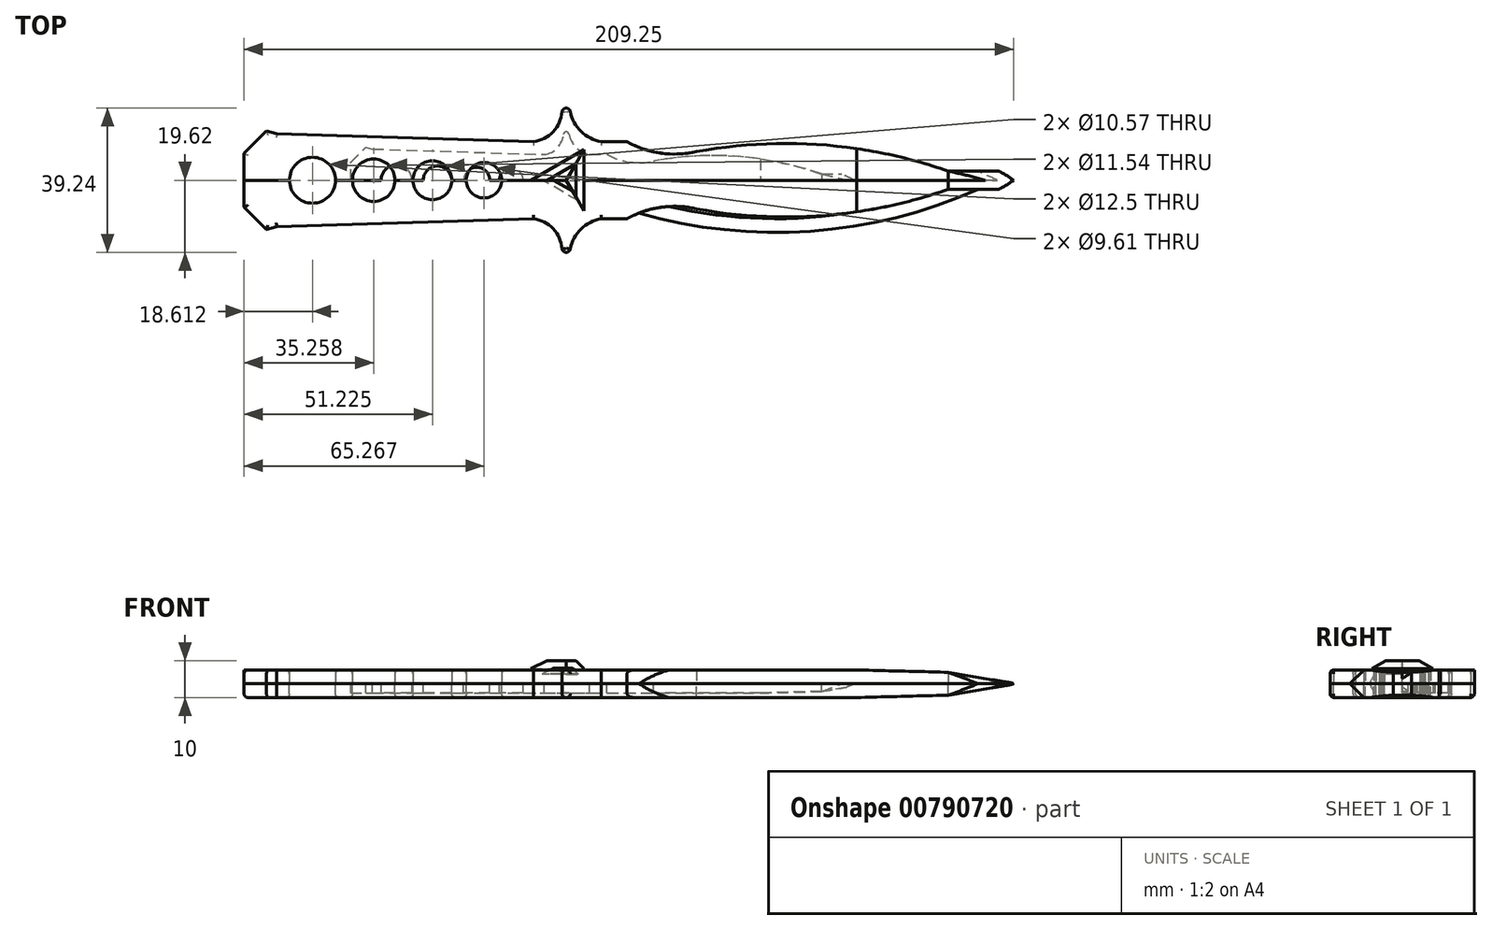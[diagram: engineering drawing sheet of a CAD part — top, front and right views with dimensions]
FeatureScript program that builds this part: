
annotation { "Feature Type Name" : "Feature", "Feature Type Description" : "" }
export const myFeature = defineFeature(function(context is Context, id is Id, definition is map)
    precondition{}
    {
        {
            var Q0;
            Q0=qCreatedBy(makeId("Top.planeOp"),FACE);
            var sketch = newSketch(context, id + "F0", { "sketchPlane" : qUnion([Q0])});
            skLineSegment(sketch, "E0", {"start": v(-58.41, -4.85) * mm, "end": v(-54.33, -8.93) * mm});
            skLineSegment(sketch, "E1", {"start": v(-54.33, -8.93) * mm, "end": v(-52.47, -8.46) * mm});
            skLineSegment(sketch, "E2", {"start": v(-52.47, -8.46) * mm, "end": v(-5.93, -6.97) * mm});
            skArc(sketch, "E3", {"start": v(-0.76, -12.46) * mm, "mid": v(-2.37, -8.8) * mm, "end": v(-5.93, -6.97) * mm});
            skArc(sketch, "E4", {"start": v(-0.76, -12.46) * mm, "mid": v(0, -13.08) * mm, "end": v(0.74, -12.46) * mm});
            skArc(sketch, "E5", {"start": v(6.37, -6.97) * mm, "mid": v(2.7, -8.83) * mm, "end": v(0.74, -12.46) * mm});
            skLineSegment(sketch, "E6", {"start": v(6.37, -6.97) * mm, "end": v(11.01, -6.97) * mm});
            skArc(sketch, "E7", {"start": v(11.01, -6.97) * mm, "mid": v(47, -10.62) * mm, "end": v(81.59, 0) * mm});
            skArc(sketch, "E8", {"start": v(23.62, -5.18) * mm, "mid": v(17.15, -4.91) * mm, "end": v(11.01, -6.97) * mm});
            skArc(sketch, "E9", {"start": v(23.62, -5.18) * mm, "mid": v(46.65, -6.4) * mm, "end": v(69.21, -1.65) * mm});
            skLineSegment(sketch, "E10", {"start": v(0, -13.08) * mm, "end": v(0, 0) * mm, "construction": true});
            skLineSegment(sketch, "E11", {"start": v(-58.41, 0) * mm, "end": v(-58.41, -4.85) * mm});
            skLineSegment(sketch, "E12", {"start": v(-58.41, 0) * mm, "end": v(81.59, 0) * mm});
            skPoint(sketch, "E13.middle", {"position": v(0, 0) * mm});
            skLineSegment(sketch, "E14", {"start": v(69.21, -1.65) * mm, "end": v(78.39, -1.66) * mm});
            skArc(sketch, "E15.MirrorCS", {"start": v(-0.76, 12.46) * mm, "mid": v(0, 13.08) * mm, "end": v(0.74, 12.46) * mm});
            skLineSegment(sketch, "E16.MirrorCS", {"start": v(-58.41, 0) * mm, "end": v(-58.41, 4.85) * mm});
            skLineSegment(sketch, "E17.MirrorCS", {"start": v(-54.33, 8.93) * mm, "end": v(-52.47, 8.46) * mm});
            skLineSegment(sketch, "E18.MirrorCS", {"start": v(6.37, 6.97) * mm, "end": v(11.01, 6.97) * mm});
            skArc(sketch, "E19.MirrorCS", {"start": v(11.01, 6.97) * mm, "mid": v(47, 10.62) * mm, "end": v(81.59, 0) * mm});
            skLineSegment(sketch, "E20.MirrorCS", {"start": v(-52.47, 8.46) * mm, "end": v(-5.93, 6.97) * mm});
            skArc(sketch, "E21.MirrorCS", {"start": v(6.37, 6.97) * mm, "mid": v(2.7, 8.83) * mm, "end": v(0.74, 12.46) * mm});
            skLineSegment(sketch, "E22.MirrorCS", {"start": v(0, 13.08) * mm, "end": v(0, 0) * mm, "construction": true});
            skArc(sketch, "E23.MirrorCS", {"start": v(-0.76, 12.46) * mm, "mid": v(-2.37, 8.8) * mm, "end": v(-5.93, 6.97) * mm});
            skArc(sketch, "E24.MirrorCS", {"start": v(23.62, 5.18) * mm, "mid": v(46.65, 6.4) * mm, "end": v(69.21, 1.65) * mm});
            skArc(sketch, "E25.MirrorCS", {"start": v(23.62, 5.18) * mm, "mid": v(17.15, 4.91) * mm, "end": v(11.01, 6.97) * mm});
            skLineSegment(sketch, "E26.MirrorCS", {"start": v(69.21, 1.65) * mm, "end": v(78.39, 1.66) * mm});
            skLineSegment(sketch, "E27.MirrorCS", {"start": v(-58.41, 4.85) * mm, "end": v(-54.33, 8.93) * mm});
            skCircle(sketch, "E28", {"center": v(-46, 0) * mm, "radius": 4.17 * mm});
            skCircle(sketch, "E29", {"center": v(-34.9, 0) * mm, "radius": 3.85 * mm});
            skCircle(sketch, "E30", {"center": v(-24.26, 0) * mm, "radius": 3.52 * mm});
            skCircle(sketch, "E31", {"center": v(-14.9, 0) * mm, "radius": 3.2 * mm});
            skSolve(sketch);
        }
        {
            var Q0;
            {var subQ1=sQuery(id+"F0.wireOp",EDGE,"E12");Q0=makeQuery(id+"F0.imprint","IMPRINT",FACE,{"disambiguationData":[TD([[makeQuery(id+"F0.imprint","IMPRINT",EDGE,{"derivedFrom":subQ1}),1.0]])]});}
            var Q1;
            Q1=makeQuery(id+"F0.imprint","IMPRINT",FACE,{"disambiguationData":[TD([[makeQuery(id+"F0.imprint","IMPRINT",EDGE,{"derivedFrom":sQuery(id+"F0.wireOp",EDGE,"E0")}),1.0]])]});
            extrude(context, id + "F1", {"entities" : qUnion([Q0, Q1]), "depth" : 2.5 * mm, "offsetDistance" : 25 * mm});
        }
        {
            var Q0;
            {var subQ0=sQuery(id+"F0.wireOp",EDGE,"E8");Q0=makeQuery(id+"F0.imprint","IMPRINT",FACE,{"disambiguationData":[TD([[makeQuery(id+"F0.imprint","IMPRINT",EDGE,{"derivedFrom":subQ0}),1.0]])]});}
            var Q1;
            Q1=makeQuery(id+"F0.imprint","IMPRINT",FACE,{"disambiguationData":[TD([[makeQuery(id+"F0.imprint","IMPRINT",EDGE,{"derivedFrom":sQuery(id+"F0.wireOp",EDGE,"E24.MirrorCS")}),1.0]])]});
            extrude(context, id + "F2", {"entities" : qUnion([Q0, Q1]), "depth" : 2.5 * mm, "offsetDistance" : 25 * mm});
        }
        {
            var Q0;
            Q0=makeQuery(id+"F2.opExtrude","CAP_EDGE",EDGE,{"disambiguationData":[OSD([sQuery(id+"F0.wireOp",EDGE,"E7")])],"isStart":false});
            var Q1;
            Q1=makeQuery(id+"F2.opExtrude","CAP_EDGE",EDGE,{"disambiguationData":[OSD([sQuery(id+"F0.wireOp",EDGE,"E19.MirrorCS")])],"isStart":false});
            chamfer(context, id + "F3", {"entities" : qUnion([Q0, Q1]), "width" : 4.1 * mm, "tangentPropagation" : true});
        }
        {
            var Q0;
            Q0=makeQuery(id+"F1.opExtrude","CAP_EDGE",EDGE,{"disambiguationData":[OSD([sQuery(id+"F0.wireOp",EDGE,"E28")])],"isStart":false});
            var Q1;
            Q1=makeQuery(id+"F1.opExtrude","CAP_EDGE",EDGE,{"disambiguationData":[OSD([sQuery(id+"F0.wireOp",EDGE,"E29")])],"isStart":false});
            var Q2;
            Q2=makeQuery(id+"F1.opExtrude","CAP_EDGE",EDGE,{"disambiguationData":[OSD([sQuery(id+"F0.wireOp",EDGE,"E30")])],"isStart":false});
            var Q3;
            Q3=makeQuery(id+"F1.opExtrude","CAP_EDGE",EDGE,{"disambiguationData":[OSD([sQuery(id+"F0.wireOp",EDGE,"E31")])],"isStart":false});
            var Q4;
            Q4=makeQuery(id+"F1.opExtrude","CAP_EDGE",EDGE,{"disambiguationData":[OSD([sQuery(id+"F0.wireOp",EDGE,"E0")])],"isStart":false});
            var Q5;
            Q5=makeQuery(id+"F1.opExtrude","CAP_EDGE",EDGE,{"disambiguationData":[OSD([sQuery(id+"F0.wireOp",EDGE,"E11"),sQuery(id+"F0.wireOp",EDGE,"E16.MirrorCS")])],"isStart":false});
            var Q6;
            Q6=makeQuery(id+"F1.opExtrude","CAP_EDGE",EDGE,{"disambiguationData":[OSD([sQuery(id+"F0.wireOp",EDGE,"E27.MirrorCS")])],"isStart":false});
            var Q7;
            Q7=makeQuery(id+"F1.opExtrude","CAP_EDGE",EDGE,{"disambiguationData":[OSD([sQuery(id+"F0.wireOp",EDGE,"E17.MirrorCS")])],"isStart":false});
            var Q8;
            Q8=makeQuery(id+"F1.opExtrude","CAP_EDGE",EDGE,{"disambiguationData":[OSD([sQuery(id+"F0.wireOp",EDGE,"E20.MirrorCS")])],"isStart":false});
            var Q9;
            Q9=makeQuery(id+"F1.opExtrude","CAP_EDGE",EDGE,{"disambiguationData":[OSD([sQuery(id+"F0.wireOp",EDGE,"E2")])],"isStart":false});
            var Q10;
            Q10=makeQuery(id+"F1.opExtrude","CAP_EDGE",EDGE,{"disambiguationData":[OSD([sQuery(id+"F0.wireOp",EDGE,"E1")])],"isStart":false});
            var Q11;
            Q11=makeQuery(id+"F1.opExtrude","CAP_EDGE",EDGE,{"disambiguationData":[OSD([sQuery(id+"F0.wireOp",EDGE,"E3")])],"isStart":false});
            var Q12;
            Q12=makeQuery(id+"F1.opExtrude","CAP_EDGE",EDGE,{"disambiguationData":[OSD([sQuery(id+"F0.wireOp",EDGE,"E5")])],"isStart":false});
            var Q13;
            Q13=makeQuery(id+"F1.opExtrude","CAP_EDGE",EDGE,{"disambiguationData":[OSD([sQuery(id+"F0.wireOp",EDGE,"E6")])],"isStart":false});
            var Q14;
            Q14=makeQuery(id+"F1.opExtrude","CAP_EDGE",EDGE,{"disambiguationData":[OSD([sQuery(id+"F0.wireOp",EDGE,"E23.MirrorCS")])],"isStart":false});
            var Q15;
            Q15=makeQuery(id+"F1.opExtrude","CAP_EDGE",EDGE,{"disambiguationData":[OSD([sQuery(id+"F0.wireOp",EDGE,"E15.MirrorCS")])],"isStart":false});
            var Q16;
            Q16=makeQuery(id+"F1.opExtrude","CAP_EDGE",EDGE,{"disambiguationData":[OSD([sQuery(id+"F0.wireOp",EDGE,"E21.MirrorCS")])],"isStart":false});
            var Q17;
            Q17=makeQuery(id+"F1.opExtrude","CAP_EDGE",EDGE,{"disambiguationData":[OSD([sQuery(id+"F0.wireOp",EDGE,"E4")])],"isStart":false});
            var Q18;
            Q18=makeQuery(id+"F1.opExtrude","CAP_EDGE",EDGE,{"disambiguationData":[OSD([sQuery(id+"F0.wireOp",EDGE,"E18.MirrorCS")])],"isStart":false});
            fillet(context, id + "F4", {"entities" : qUnion([Q0, Q1, Q2, Q3, Q4, Q5, Q6, Q7, Q8, Q9, Q10, Q11, Q12, Q13, Q14, Q15, Q16, Q17, Q18]), "radius" : 0.7 * mm, "tangentPropagation" : true, "allowEdgeOverflow" : false});
        }
        {
            var Q0;
            Q0=makeQuery(id+"F2.opExtrude","SWEPT_BODY",BODY,{"disambiguationData":[OSD([sQuery(id+"F0.wireOp",EDGE,"E19.MirrorCS"),sQuery(id+"F0.wireOp",EDGE,"E24.MirrorCS"),sQuery(id+"F0.wireOp",EDGE,"E25.MirrorCS"),sQuery(id+"F0.wireOp",EDGE,"E26.MirrorCS")])]});
            var Q1;
            Q1=makeQuery(id+"F2.opExtrude","SWEPT_BODY",BODY,{"disambiguationData":[OSD([sQuery(id+"F0.wireOp",EDGE,"E7"),sQuery(id+"F0.wireOp",EDGE,"E8"),sQuery(id+"F0.wireOp",EDGE,"E9"),sQuery(id+"F0.wireOp",EDGE,"E14")])]});
            var Q2;
            Q2=makeQuery(id+"F1.opExtrude","SWEPT_BODY",BODY,{"disambiguationData":[OSD([sQuery(id+"F0.wireOp",EDGE,"E0"),sQuery(id+"F0.wireOp",EDGE,"E1"),sQuery(id+"F0.wireOp",EDGE,"E2"),sQuery(id+"F0.wireOp",EDGE,"E3"),sQuery(id+"F0.wireOp",EDGE,"E4"),sQuery(id+"F0.wireOp",EDGE,"E5"),sQuery(id+"F0.wireOp",EDGE,"E6"),sQuery(id+"F0.wireOp",EDGE,"E7"),sQuery(id+"F0.wireOp",EDGE,"E8"),sQuery(id+"F0.wireOp",EDGE,"E9"),sQuery(id+"F0.wireOp",EDGE,"E11"),sQuery(id+"F0.wireOp",EDGE,"E14"),sQuery(id+"F0.wireOp",EDGE,"E15.MirrorCS"),sQuery(id+"F0.wireOp",EDGE,"E16.MirrorCS"),sQuery(id+"F0.wireOp",EDGE,"E17.MirrorCS"),sQuery(id+"F0.wireOp",EDGE,"E18.MirrorCS"),sQuery(id+"F0.wireOp",EDGE,"E19.MirrorCS"),sQuery(id+"F0.wireOp",EDGE,"E20.MirrorCS"),sQuery(id+"F0.wireOp",EDGE,"E21.MirrorCS"),sQuery(id+"F0.wireOp",EDGE,"E23.MirrorCS"),sQuery(id+"F0.wireOp",EDGE,"E24.MirrorCS"),sQuery(id+"F0.wireOp",EDGE,"E25.MirrorCS"),sQuery(id+"F0.wireOp",EDGE,"E26.MirrorCS"),sQuery(id+"F0.wireOp",EDGE,"E27.MirrorCS"),sQuery(id+"F0.wireOp",EDGE,"E28"),sQuery(id+"F0.wireOp",EDGE,"E29"),sQuery(id+"F0.wireOp",EDGE,"E30"),sQuery(id+"F0.wireOp",EDGE,"E31"),sQuery(id+"F0.wireOp",EDGE,"IPMrH8It-OBRR-uF5r-pI5p-KHMHURjL3cqm")])]});
            var Q3;
            Q3=sQuery(id+"F0.wireOp",VERTEX,"E13.middle");
            transform(context, id + "F5", {"entities" : qUnion([Q0, Q1, Q2]), "transformType" : TransformType.SCALE_UNIFORMLY, "scale" : 1.5, "scalePoint" : qUnion([Q3]), "makeCopy" : false});
        }
        {
            var Q0;
            Q0=makeQuery(id+"F1.opExtrude","CAP_FACE",FACE,{"disambiguationData":[OSD([sQuery(id+"F0.wireOp",EDGE,"E0"),sQuery(id+"F0.wireOp",EDGE,"E1"),sQuery(id+"F0.wireOp",EDGE,"E2"),sQuery(id+"F0.wireOp",EDGE,"E3"),sQuery(id+"F0.wireOp",EDGE,"E4"),sQuery(id+"F0.wireOp",EDGE,"E5"),sQuery(id+"F0.wireOp",EDGE,"E6"),sQuery(id+"F0.wireOp",EDGE,"E7"),sQuery(id+"F0.wireOp",EDGE,"E8"),sQuery(id+"F0.wireOp",EDGE,"E9"),sQuery(id+"F0.wireOp",EDGE,"E11"),sQuery(id+"F0.wireOp",EDGE,"E14"),sQuery(id+"F0.wireOp",EDGE,"E15.MirrorCS"),sQuery(id+"F0.wireOp",EDGE,"E16.MirrorCS"),sQuery(id+"F0.wireOp",EDGE,"E17.MirrorCS"),sQuery(id+"F0.wireOp",EDGE,"E18.MirrorCS"),sQuery(id+"F0.wireOp",EDGE,"E19.MirrorCS"),sQuery(id+"F0.wireOp",EDGE,"E20.MirrorCS"),sQuery(id+"F0.wireOp",EDGE,"E21.MirrorCS"),sQuery(id+"F0.wireOp",EDGE,"E23.MirrorCS"),sQuery(id+"F0.wireOp",EDGE,"E24.MirrorCS"),sQuery(id+"F0.wireOp",EDGE,"E25.MirrorCS"),sQuery(id+"F0.wireOp",EDGE,"E26.MirrorCS"),sQuery(id+"F0.wireOp",EDGE,"E27.MirrorCS"),sQuery(id+"F0.wireOp",EDGE,"E28"),sQuery(id+"F0.wireOp",EDGE,"E29"),sQuery(id+"F0.wireOp",EDGE,"E30"),sQuery(id+"F0.wireOp",EDGE,"E31")])],"isStart":false});
            var sketch = newSketch(context, id + "F6", { "sketchPlane" : qUnion([Q0])});
            skCircle(sketch, "E32.cCircle", {"center": v(0, 0) * mm, "radius": 9.61 * mm, "construction": true});
            skLineSegment(sketch, "E32.0", {"start": v(-9.61, 0) * mm, "end": v(4.8, 8.33) * mm});
            skLineSegment(sketch, "E32.1", {"start": v(4.8, 8.33) * mm, "end": v(4.8, -8.33) * mm});
            skLineSegment(sketch, "E32.2", {"start": v(4.8, -8.33) * mm, "end": v(-9.61, 0) * mm});
            skLineSegment(sketch, "E33", {"start": v(4.8, 8.33) * mm, "end": v(0, 0) * mm});
            skLineSegment(sketch, "E34", {"start": v(0, 0) * mm, "end": v(4.8, -8.33) * mm});
            skLineSegment(sketch, "E35", {"start": v(0, 0) * mm, "end": v(-9.61, 0) * mm});
            skSolve(sketch);
        }
        {
            var Q0;
            Q0=makeQuery(id+"F6.imprint","IMPRINT",FACE,{"disambiguationData":[TD([[makeQuery(id+"F6.imprint","IMPRINT",EDGE,{"derivedFrom":sQuery(id+"F6.wireOp",EDGE,"E32.0")}),-1.0]])]});
            extrude(context, id + "F7", {"entities" : qUnion([Q0]), "depth" : 2.5 * mm, "offsetDistance" : 25 * mm});
        }
        {
            var Q0;
            Q0=makeQuery(id+"F6.imprint","IMPRINT",FACE,{"disambiguationData":[TD([[makeQuery(id+"F6.imprint","IMPRINT",EDGE,{"derivedFrom":sQuery(id+"F6.wireOp",EDGE,"E32.1")}),-1.0]])]});
            extrude(context, id + "F8", {"entities" : qUnion([Q0]), "depth" : 2.5 * mm, "offsetDistance" : 25 * mm});
        }
        {
            var Q0;
            Q0=makeQuery(id+"F6.imprint","IMPRINT",FACE,{"disambiguationData":[TD([[makeQuery(id+"F6.imprint","IMPRINT",EDGE,{"derivedFrom":sQuery(id+"F6.wireOp",EDGE,"E32.2")}),-1.0]])]});
            extrude(context, id + "F9", {"entities" : qUnion([Q0]), "depth" : 2.5 * mm, "offsetDistance" : 25 * mm});
        }
        {
            var Q0;
            Q0=makeQuery(id+"F8.opExtrude","CAP_EDGE",EDGE,{"disambiguationData":[OSD([sQuery(id+"F6.wireOp",EDGE,"E32.1")])],"isStart":false});
            var Q1;
            Q1=makeQuery(id+"F7.opExtrude","CAP_EDGE",EDGE,{"disambiguationData":[OSD([sQuery(id+"F6.wireOp",EDGE,"E32.0")])],"isStart":false});
            var Q2;
            Q2=makeQuery(id+"F9.opExtrude","CAP_EDGE",EDGE,{"disambiguationData":[OSD([sQuery(id+"F6.wireOp",EDGE,"E32.2")])],"isStart":false});
            chamfer(context, id + "F10", {"entities" : qUnion([Q0, Q1, Q2]), "width" : 2.2 * mm, "tangentPropagation" : true});
        }
        {
            var Q0;
            Q0=makeQuery(id+"F9.opExtrude","CAP_FACE",FACE,{"disambiguationData":[OSD([sQuery(id+"F6.wireOp",EDGE,"E32.2"),sQuery(id+"F6.wireOp",EDGE,"E34"),sQuery(id+"F6.wireOp",EDGE,"E35")])],"isStart":false});
            cPlane(context, id + "F11", {"entities" : qUnion([Q0]), "cplaneType" : CPlaneType.OFFSET, "offset" : 0 * mm, "oppositeDirection" : true, "width" : 150 * mm, "height" : 150 * mm});
        }
        {
            var Q0;
            Q0=qCreatedBy(id+"F11.planeOp",FACE);
            var sketch = newSketch(context, id + "F12", { "sketchPlane" : qUnion([Q0])});
            skCircle(sketch, "E36.cCircle", {"center": v(0, 0) * mm, "radius": 5.21 * mm, "construction": true});
            skLineSegment(sketch, "E36.0", {"start": v(-5.21, 0) * mm, "end": v(2.6, 4.52) * mm});
            skLineSegment(sketch, "E36.1", {"start": v(2.6, 4.52) * mm, "end": v(2.6, -4.52) * mm});
            skLineSegment(sketch, "E36.2", {"start": v(2.6, -4.52) * mm, "end": v(-5.21, 0) * mm});
            skLineSegment(sketch, "E37", {"start": v(-5.21, 0) * mm, "end": v(0, 0) * mm});
            skLineSegment(sketch, "E38", {"start": v(2.6, 4.52) * mm, "end": v(0, 0) * mm});
            skLineSegment(sketch, "E39", {"start": v(0, 0) * mm, "end": v(2.6, -4.52) * mm});
            skSolve(sketch);
        }
        {
            var Q0;
            Q0=makeQuery(id+"F12.imprint","IMPRINT",FACE,{"disambiguationData":[TD([[makeQuery(id+"F12.imprint","IMPRINT",EDGE,{"derivedFrom":sQuery(id+"F12.wireOp",EDGE,"E36.2")}),-1.0]])]});
            var Q1;
            Q1=makeQuery(id+"F12.imprint","IMPRINT",FACE,{"disambiguationData":[TD([[makeQuery(id+"F12.imprint","IMPRINT",EDGE,{"derivedFrom":sQuery(id+"F12.wireOp",EDGE,"E36.1")}),-1.0]])]});
            var Q2;
            Q2=makeQuery(id+"F12.imprint","IMPRINT",FACE,{"disambiguationData":[TD([[makeQuery(id+"F12.imprint","IMPRINT",EDGE,{"derivedFrom":sQuery(id+"F12.wireOp",EDGE,"E36.0")}),-1.0]])]});
            extrude(context, id + "F13", {"entities" : qUnion([Q0, Q1, Q2]), "endBound" : BoundingType.SYMMETRIC, "oppositeDirection" : true, "depth" : 4 * mm, "offsetDistance" : 25 * mm});
        }
        {
            var Q0;
            Q0=makeQuery(id+"F13.opExtrude","CAP_EDGE",EDGE,{"disambiguationData":[OSD([sQuery(id+"F12.wireOp",EDGE,"E36.0")])],"isStart":false});
            var Q1;
            Q1=makeQuery(id+"F13.opExtrude","CAP_EDGE",EDGE,{"disambiguationData":[OSD([sQuery(id+"F12.wireOp",EDGE,"E36.2")])],"isStart":false});
            var Q2;
            Q2=makeQuery(id+"F13.opExtrude","CAP_EDGE",EDGE,{"disambiguationData":[OSD([sQuery(id+"F12.wireOp",EDGE,"E36.1")])],"isStart":false});
            chamfer(context, id + "F14", {"entities" : qUnion([Q0, Q1, Q2]), "width" : 2.6 * mm, "tangentPropagation" : true});
        }
        {
            var Q0;
            Q0=makeQuery(id+"F13.opExtrude","SWEPT_BODY",BODY,{"disambiguationData":[OSD([sQuery(id+"F12.wireOp",EDGE,"E36.0"),sQuery(id+"F12.wireOp",EDGE,"E36.1"),sQuery(id+"F12.wireOp",EDGE,"E36.2")])]});
            var Q1;
            Q1=qCreatedBy(makeId("Origin.pointOp"),VERTEX);
            transform(context, id + "F15", {"entities" : qUnion([Q0]), "transformType" : TransformType.SCALE_UNIFORMLY, "scale" : 1.6, "scalePoint" : qUnion([Q1]), "makeCopy" : false});
        }
        {
            var Q0;
            Q0=makeQuery(id+"F13.opExtrude","SWEPT_BODY",BODY,{"disambiguationData":[OSD([sQuery(id+"F12.wireOp",EDGE,"E36.0"),sQuery(id+"F12.wireOp",EDGE,"E36.1"),sQuery(id+"F12.wireOp",EDGE,"E36.2")])]});
            transform(context, id + "F16", {"entities" : qUnion([Q0]), "transformType" : TransformType.TRANSLATION_3D, "dx" : 0 * mm, "dy" : 0 * mm, "dz" : -3 * mm, "makeCopy" : false});
        }
        {
            var Q0;
            Q0=makeQuery(id+"F13.opExtrude","SWEPT_BODY",BODY,{"disambiguationData":[OSD([sQuery(id+"F12.wireOp",EDGE,"E36.0"),sQuery(id+"F12.wireOp",EDGE,"E36.1"),sQuery(id+"F12.wireOp",EDGE,"E36.2")])]});
            var Q1;
            Q1=makeQuery(id+"F9.opExtrude","SWEPT_BODY",BODY,{"disambiguationData":[OSD([sQuery(id+"F6.wireOp",EDGE,"E32.2"),sQuery(id+"F6.wireOp",EDGE,"E34"),sQuery(id+"F6.wireOp",EDGE,"E35")])]});
            booleanBodies(context, id + "F17", {"operationType" : BooleanOperationType.SUBTRACTION, "tools" : qUnion([Q0]), "targets" : qUnion([Q1])});
        }
        {
            var Q0;
            Q0=qCreatedBy(makeId("Front.planeOp"),FACE);
            var sketch = newSketch(context, id + "F18", { "sketchPlane" : qUnion([Q0])});
            skPoint(sketch, "E40", {"position": v(103.82, 3.11) * mm});
            skPoint(sketch, "E41", {"position": v(79.01, 3.75) * mm});
            skPoint(sketch, "E42", {"position": v(140.36, 0) * mm});
            skPoint(sketch, "E43", {"position": v(134.72, 19.24) * mm});
            skPoint(sketch, "E44", {"position": v(113.07, 12.07) * mm});
            skPoint(sketch, "E45", {"position": v(113.53, 22.44) * mm});
            skPoint(sketch, "E46", {"position": v(120.54, 18.48) * mm});
            skPoint(sketch, "E47", {"position": v(118.26, 28.54) * mm});
            skPoint(sketch, "E48", {"position": v(109.1, 26.4) * mm});
            skPoint(sketch, "E49", {"position": v(99.05, 19.09) * mm});
            skPoint(sketch, "E50", {"position": v(92.03, 14.97) * mm});
            skLineSegment(sketch, "E51", {"start": v(79.01, 3.75) * mm, "end": v(103.82, 3.11) * mm});
            skLineSegment(sketch, "E52", {"start": v(140.36, 0) * mm, "end": v(134.72, 19.24) * mm});
            skLineSegment(sketch, "E53", {"start": v(134.72, 19.24) * mm, "end": v(113.07, 12.07) * mm});
            skLineSegment(sketch, "E54", {"start": v(113.07, 12.07) * mm, "end": v(113.53, 22.44) * mm});
            skLineSegment(sketch, "E55", {"start": v(113.53, 22.44) * mm, "end": v(120.54, 18.48) * mm});
            skLineSegment(sketch, "E56", {"start": v(120.54, 18.48) * mm, "end": v(118.26, 28.54) * mm});
            skLineSegment(sketch, "E57", {"start": v(118.26, 28.54) * mm, "end": v(109.1, 26.4) * mm});
            skLineSegment(sketch, "E58", {"start": v(109.1, 26.4) * mm, "end": v(99.05, 19.09) * mm});
            skLineSegment(sketch, "E59", {"start": v(99.05, 19.09) * mm, "end": v(92.03, 14.97) * mm});
            skLineSegment(sketch, "E60", {"start": v(92.03, 14.97) * mm, "end": v(79.01, 3.75) * mm});
            skPoint(sketch, "E61", {"position": v(122.38, 0) * mm});
            skLineSegment(sketch, "E62", {"start": v(103.82, 3.11) * mm, "end": v(122.38, 0) * mm});
            skLineSegment(sketch, "E63", {"start": v(122.38, 0) * mm, "end": v(140.36, 0) * mm});
            skSolve(sketch);
        }
        {
            var Q0;
            Q0 = qSketchRegion(id + "F18", true);
            extrude(context, id + "F19", {"entities" : qUnion([Q0]), "operationType" : NewBodyOperationType.REMOVE, "endBound" : BoundingType.SYMMETRIC, "oppositeDirection" : true, "depth" : 25 * mm, "offsetDistance" : 25 * mm});
        }
        {
            var Q0;
            Q0=makeQuery(id+"F19.boolean.opBoolean","INTERSECT",EDGE,{"derivedFrom":[makeQuery(id+"F1.opExtrude","SWEPT_FACE",FACE,{"disambiguationData":[OSD([sQuery(id+"F0.wireOp",EDGE,"E19.MirrorCS")])]}),makeQuery(id+"F19.opExtrude","SWEPT_FACE",FACE,{"disambiguationData":[OSD([sQuery(id+"F18.wireOp",EDGE,"E62")])]})]});
            var Q1;
            Q1=makeQuery(id+"F19.boolean.opBoolean","INTERSECT",EDGE,{"derivedFrom":[makeQuery(id+"F1.opExtrude","SWEPT_FACE",FACE,{"disambiguationData":[OSD([sQuery(id+"F0.wireOp",EDGE,"E7")])]}),makeQuery(id+"F19.opExtrude","SWEPT_FACE",FACE,{"disambiguationData":[OSD([sQuery(id+"F18.wireOp",EDGE,"E62")])]})]});
            fillet(context, id + "F20", {"entities" : qUnion([Q0, Q1]), "radius" : 0.85 * mm, "tangentPropagation" : true, "allowEdgeOverflow" : false});
        }
        {
            var Q0;
            Q0=makeQuery(id+"F2.opExtrude","SWEPT_BODY",BODY,{"disambiguationData":[OSD([sQuery(id+"F0.wireOp",EDGE,"E19.MirrorCS"),sQuery(id+"F0.wireOp",EDGE,"E24.MirrorCS"),sQuery(id+"F0.wireOp",EDGE,"E25.MirrorCS"),sQuery(id+"F0.wireOp",EDGE,"E26.MirrorCS")])]});
            var Q1;
            Q1=makeQuery(id+"F2.opExtrude","SWEPT_BODY",BODY,{"disambiguationData":[OSD([sQuery(id+"F0.wireOp",EDGE,"E7"),sQuery(id+"F0.wireOp",EDGE,"E8"),sQuery(id+"F0.wireOp",EDGE,"E9"),sQuery(id+"F0.wireOp",EDGE,"E14")])]});
            var Q2;
            Q2=makeQuery(id+"F1.opExtrude","SWEPT_BODY",BODY,{"disambiguationData":[OSD([sQuery(id+"F0.wireOp",EDGE,"E0"),sQuery(id+"F0.wireOp",EDGE,"E1"),sQuery(id+"F0.wireOp",EDGE,"E2"),sQuery(id+"F0.wireOp",EDGE,"E3"),sQuery(id+"F0.wireOp",EDGE,"E4"),sQuery(id+"F0.wireOp",EDGE,"E5"),sQuery(id+"F0.wireOp",EDGE,"E6"),sQuery(id+"F0.wireOp",EDGE,"E7"),sQuery(id+"F0.wireOp",EDGE,"E8"),sQuery(id+"F0.wireOp",EDGE,"E9"),sQuery(id+"F0.wireOp",EDGE,"E11"),sQuery(id+"F0.wireOp",EDGE,"E14"),sQuery(id+"F0.wireOp",EDGE,"E15.MirrorCS"),sQuery(id+"F0.wireOp",EDGE,"E16.MirrorCS"),sQuery(id+"F0.wireOp",EDGE,"E17.MirrorCS"),sQuery(id+"F0.wireOp",EDGE,"E18.MirrorCS"),sQuery(id+"F0.wireOp",EDGE,"E19.MirrorCS"),sQuery(id+"F0.wireOp",EDGE,"E20.MirrorCS"),sQuery(id+"F0.wireOp",EDGE,"E21.MirrorCS"),sQuery(id+"F0.wireOp",EDGE,"E23.MirrorCS"),sQuery(id+"F0.wireOp",EDGE,"E24.MirrorCS"),sQuery(id+"F0.wireOp",EDGE,"E25.MirrorCS"),sQuery(id+"F0.wireOp",EDGE,"E26.MirrorCS"),sQuery(id+"F0.wireOp",EDGE,"E27.MirrorCS"),sQuery(id+"F0.wireOp",EDGE,"E28"),sQuery(id+"F0.wireOp",EDGE,"E29"),sQuery(id+"F0.wireOp",EDGE,"E30"),sQuery(id+"F0.wireOp",EDGE,"E31")])]});
            var Q3;
            Q3=qCreatedBy(makeId("Top.planeOp"),FACE);
            mirror(context, id + "F21", {"entities" : qUnion([Q0, Q1, Q2]), "mirrorPlane" : qUnion([Q3])});
        }
        {
            var Q0;
            Q0=makeQuery(id+"F9.opExtrude","SWEPT_BODY",BODY,{"disambiguationData":[OSD([sQuery(id+"F6.wireOp",EDGE,"E32.2"),sQuery(id+"F6.wireOp",EDGE,"E34"),sQuery(id+"F6.wireOp",EDGE,"E35")])]});
            var Q1;
            Q1=makeQuery(id+"F21.opPattern","COPY",BODY,{"derivedFrom":makeQuery(id+"F2.opExtrude","SWEPT_BODY",BODY,{"disambiguationData":[OSD([sQuery(id+"F0.wireOp",EDGE,"E19.MirrorCS"),sQuery(id+"F0.wireOp",EDGE,"E24.MirrorCS"),sQuery(id+"F0.wireOp",EDGE,"E25.MirrorCS"),sQuery(id+"F0.wireOp",EDGE,"E26.MirrorCS")])]}),"instanceName":"1"});
            var Q2;
            Q2=qCreatedBy(makeId("Origin.pointOp"),VERTEX);
            var Q3;
            Q3=qCreatedBy(makeId("Origin.pointOp"),VERTEX);
            transform(context, id + "F22", {"entities" : qUnion([Q0, Q1]), "transformType" : TransformType.SCALE_UNIFORMLY, "scale" : 0.67, "scalePoint" : qUnion([Q3]), "makeCopy" : false});
        }
    });
